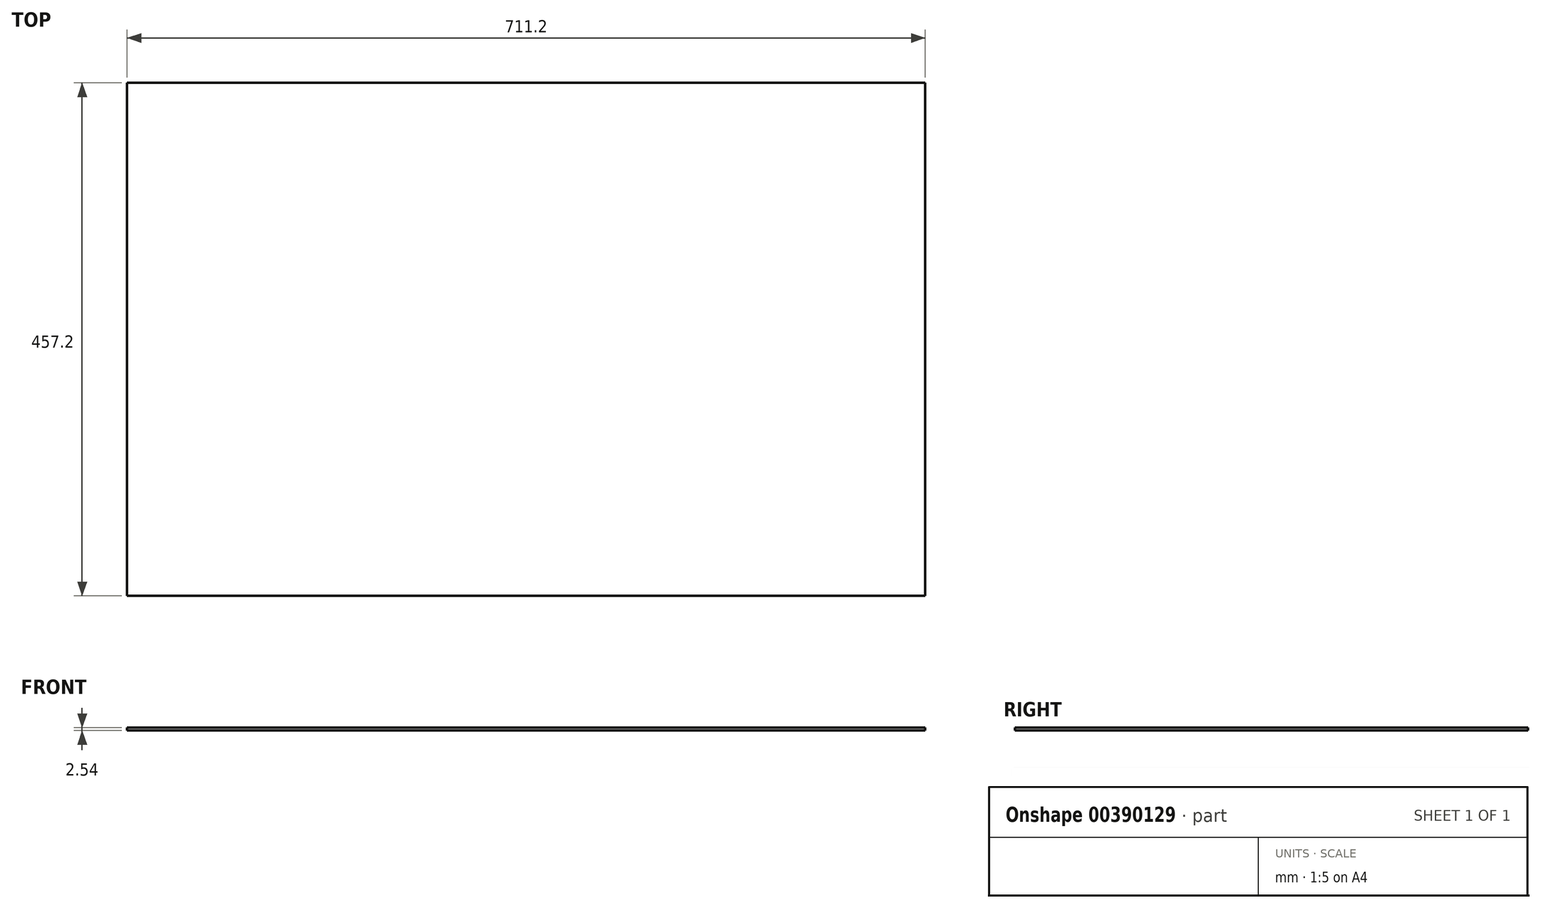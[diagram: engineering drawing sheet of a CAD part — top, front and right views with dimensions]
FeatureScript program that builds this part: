
annotation { "Feature Type Name" : "Feature", "Feature Type Description" : "" }
export const myFeature = defineFeature(function(context is Context, id is Id, definition is map)
    precondition{}
    {
        {
            var Q0;
            Q0=qCreatedBy(makeId("Top.planeOp"),FACE);
            var sketch = newSketch(context, id + "F0", { "sketchPlane" : qUnion([Q0])});
            skLineSegment(sketch, "E0.bottom", {"start": v(0, 0) * mm, "end": v(711.2, 0) * mm});
            skLineSegment(sketch, "E0.top", {"start": v(0, 457.2) * mm, "end": v(711.2, 457.2) * mm});
            skLineSegment(sketch, "E0.left", {"start": v(0, 0) * mm, "end": v(0, 457.2) * mm});
            skLineSegment(sketch, "E0.right", {"start": v(711.2, 0) * mm, "end": v(711.2, 457.2) * mm});
            skSolve(sketch);
        }
        {
            var Q0;
            Q0=makeQuery(id+"F0.imprint","IMPRINT",FACE,{"disambiguationData":[TD([[makeQuery(id+"F0.imprint","IMPRINT",EDGE,{"derivedFrom":sQuery(id+"F0.wireOp",EDGE,"E0.bottom")}),1.0]])]});
            extrude(context, id + "F1", {"entities" : qUnion([Q0]), "depth" : 2.54 * mm});
        }
    });
